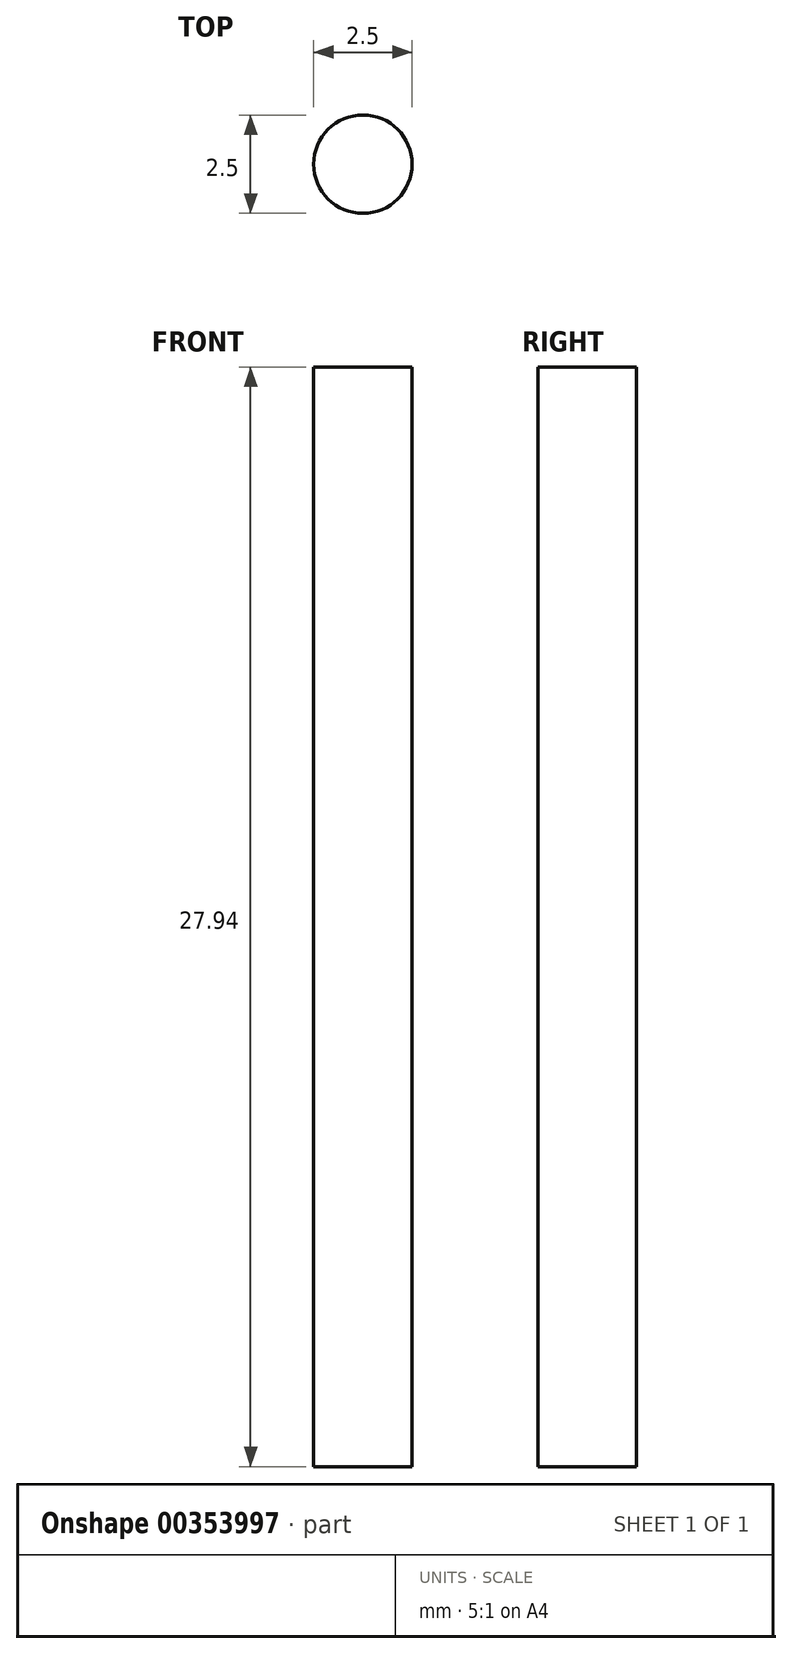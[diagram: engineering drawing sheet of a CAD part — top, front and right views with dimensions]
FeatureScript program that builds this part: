
annotation { "Feature Type Name" : "Feature", "Feature Type Description" : "" }
export const myFeature = defineFeature(function(context is Context, id is Id, definition is map)
    precondition{}
    {
        {
            var Q0;
            Q0=qCreatedBy(makeId("Top.planeOp"),FACE);
            var sketch = newSketch(context, id + "F0", { "sketchPlane" : qUnion([Q0])});
            skCircle(sketch, "E0", {"center": v(0, 0) * mm, "radius": 1.25 * mm});
            skSolve(sketch);
        }
        {
            var Q0;
            Q0 = qSketchRegion(id + "F0", true);
            extrude(context, id + "F1", {"entities" : qUnion([Q0]), "endBound" : BoundingType.SYMMETRIC, "depth" : 27.94 * mm});
        }
    });
